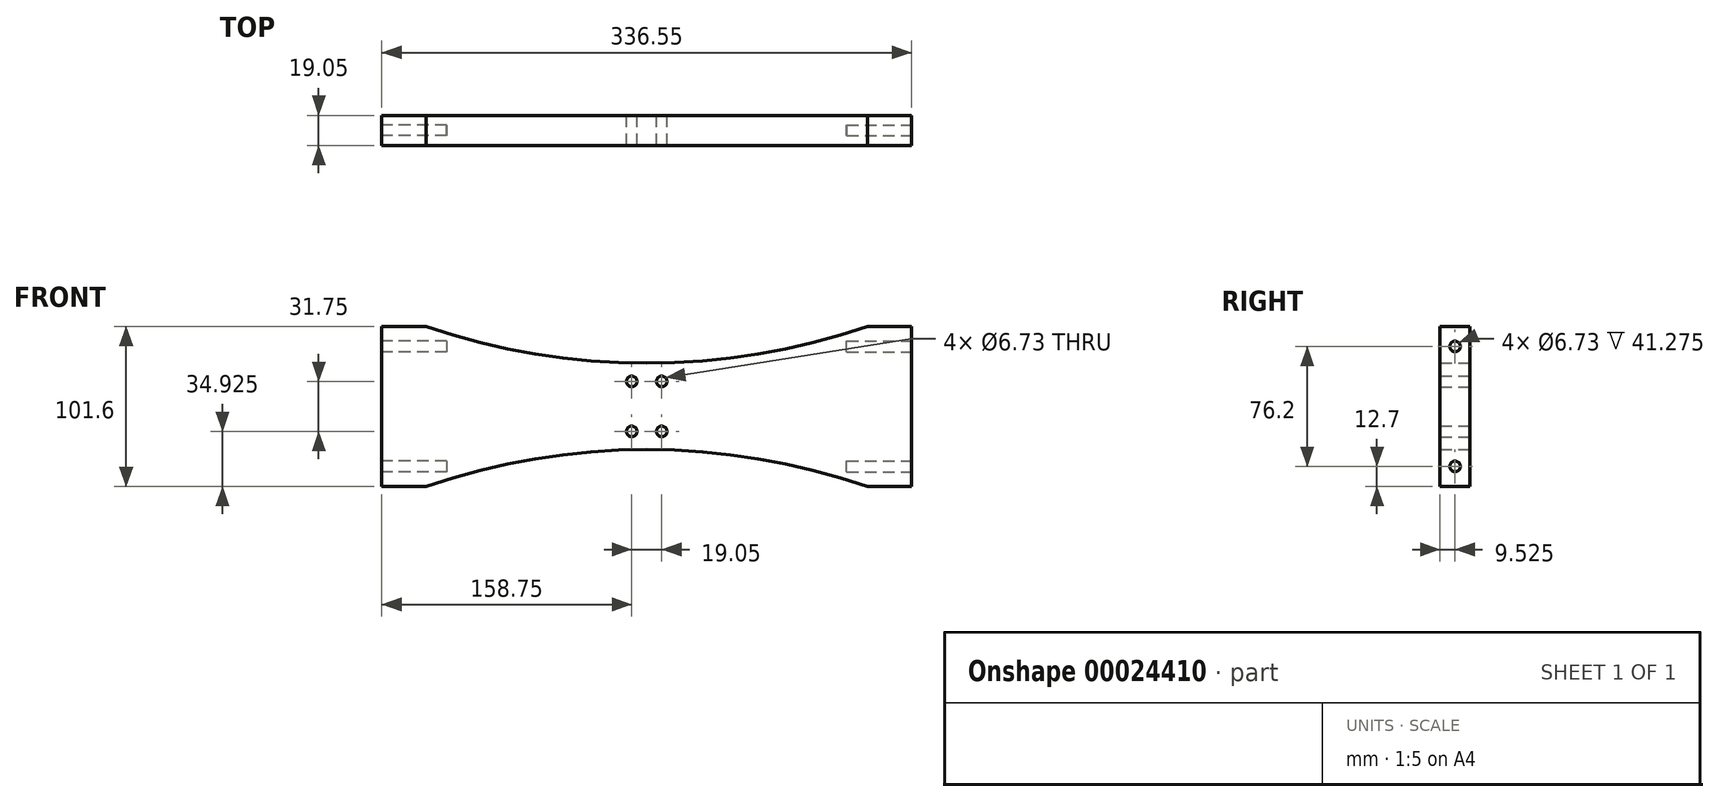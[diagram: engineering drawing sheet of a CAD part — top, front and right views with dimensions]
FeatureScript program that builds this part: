
annotation { "Feature Type Name" : "Feature", "Feature Type Description" : "" }
export const myFeature = defineFeature(function(context is Context, id is Id, definition is map)
    precondition{}
    {
        {
            var Q0;
            Q0=qCreatedBy(makeId("Front.planeOp"),FACE);
            var sketch = newSketch(context, id + "F0", { "sketchPlane" : qUnion([Q0])});
            skLineSegment(sketch, "E0.bottom", {"start": v(0, 0) * mm, "end": v(28.2, 0) * mm});
            skLineSegment(sketch, "E0.top", {"start": v(0, 101.6) * mm, "end": v(28.2, 101.6) * mm});
            skLineSegment(sketch, "E0.left", {"start": v(0, 0) * mm, "end": v(0, 101.6) * mm});
            skLineSegment(sketch, "E0.right", {"start": v(336.55, 0) * mm, "end": v(336.55, 101.6) * mm});
            skLineSegment(sketch, "E1", {"start": v(308.36, 101.6) * mm, "end": v(336.55, 101.6) * mm});
            skLineSegment(sketch, "E2", {"start": v(308.36, 0) * mm, "end": v(336.55, 0) * mm});
            skLineSegment(sketch, "E3", {"start": v(28.2, 101.6) * mm, "end": v(28.2, 0) * mm});
            skLineSegment(sketch, "E4", {"start": v(308.36, 101.6) * mm, "end": v(308.36, 0) * mm});
            skArc(sketch, "E5", {"start": v(308.36, 0) * mm, "mid": v(168.28, 23.35) * mm, "end": v(28.2, 0) * mm});
            skArc(sketch, "E6", {"start": v(28.2, 101.6) * mm, "mid": v(168.28, 78.25) * mm, "end": v(308.36, 101.6) * mm});
            skLineSegment(sketch, "E7", {"start": v(0, 50.8) * mm, "end": v(336.55, 50.8) * mm, "construction": true});
            skCircle(sketch, "E8", {"center": v(158.75, 66.68) * mm, "radius": 3.37 * mm});
            skCircle(sketch, "E9", {"center": v(177.8, 66.68) * mm, "radius": 3.37 * mm});
            skCircle(sketch, "E10", {"center": v(158.75, 34.92) * mm, "radius": 3.37 * mm});
            skCircle(sketch, "E11", {"center": v(177.8, 34.92) * mm, "radius": 3.37 * mm});
            skLineSegment(sketch, "E12", {"start": v(168.28, 50.8) * mm, "end": v(168.28, 34.93) * mm, "construction": true});
            skLineSegment(sketch, "E13", {"start": v(158.75, 66.68) * mm, "end": v(177.8, 66.68) * mm, "construction": true});
            skLineSegment(sketch, "E14", {"start": v(177.8, 66.68) * mm, "end": v(177.8, 50.8) * mm, "construction": true});
            skLineSegment(sketch, "E15", {"start": v(158.75, 34.93) * mm, "end": v(177.8, 34.93) * mm, "construction": true});
            skLineSegment(sketch, "E16", {"start": v(158.75, 66.68) * mm, "end": v(158.75, 34.92) * mm, "construction": true});
            skLineSegment(sketch, "E17", {"start": v(177.8, 50.8) * mm, "end": v(177.8, 34.92) * mm, "construction": true});
            skSolve(sketch);
        }
        {
            var Q0;
            Q0 = qSketchRegion(id + "F0", true);
            extrude(context, id + "F1", {"entities" : qUnion([Q0]), "depth" : 19.05 * mm});
        }
        {
            var Q0;
            Q0=makeQuery(id+"F1.opExtrude","SWEPT_FACE",FACE,{"disambiguationData":[OSD([sQuery(id+"F0.wireOp",EDGE,"E0.right")])]});
            var sketch = newSketch(context, id + "F2", { "sketchPlane" : qUnion([Q0])});
            skCircle(sketch, "E18", {"center": v(-9.53, 88.9) * mm, "radius": 3.37 * mm});
            skCircle(sketch, "E19", {"center": v(-9.52, 12.7) * mm, "radius": 3.37 * mm});
            skLineSegment(sketch, "E20", {"start": v(-9.53, 0) * mm, "end": v(-9.53, 101.6) * mm, "construction": true});
            skSolve(sketch);
        }
        {
            var Q0;
            Q0=makeQuery(id+"F2.imprint","IMPRINT",FACE,{"disambiguationData":[TD([[makeQuery(id+"F2.imprint","IMPRINT",EDGE,{"derivedFrom":sQuery(id+"F2.wireOp",EDGE,"E18")}),1.0]])]});
            var Q1;
            Q1=makeQuery(id+"F2.imprint","IMPRINT",FACE,{"disambiguationData":[TD([[makeQuery(id+"F2.imprint","IMPRINT",EDGE,{"derivedFrom":sQuery(id+"F2.wireOp",EDGE,"E19")}),1.0]])]});
            extrude(context, id + "F3", {"entities" : qUnion([Q0, Q1]), "operationType" : NewBodyOperationType.REMOVE, "oppositeDirection" : true, "depth" : 41.27 * mm});
        }
        {
            var Q0;
            Q0=makeQuery(id+"F1.opExtrude","SWEPT_FACE",FACE,{"disambiguationData":[OSD([sQuery(id+"F0.wireOp",EDGE,"E0.left")])]});
            var sketch = newSketch(context, id + "F4", { "sketchPlane" : qUnion([Q0])});
            skLineSegment(sketch, "E21", {"start": v(9.53, 0) * mm, "end": v(9.53, 101.6) * mm, "construction": true});
            skCircle(sketch, "E22", {"center": v(9.53, 88.9) * mm, "radius": 3.37 * mm});
            skCircle(sketch, "E23", {"center": v(9.53, 12.7) * mm, "radius": 3.37 * mm});
            skSolve(sketch);
        }
        {
            var Q0;
            Q0 = qSketchRegion(id + "F4", true);
            extrude(context, id + "F5", {"entities" : qUnion([Q0]), "operationType" : NewBodyOperationType.REMOVE, "oppositeDirection" : true, "depth" : 41.27 * mm});
        }
    });
